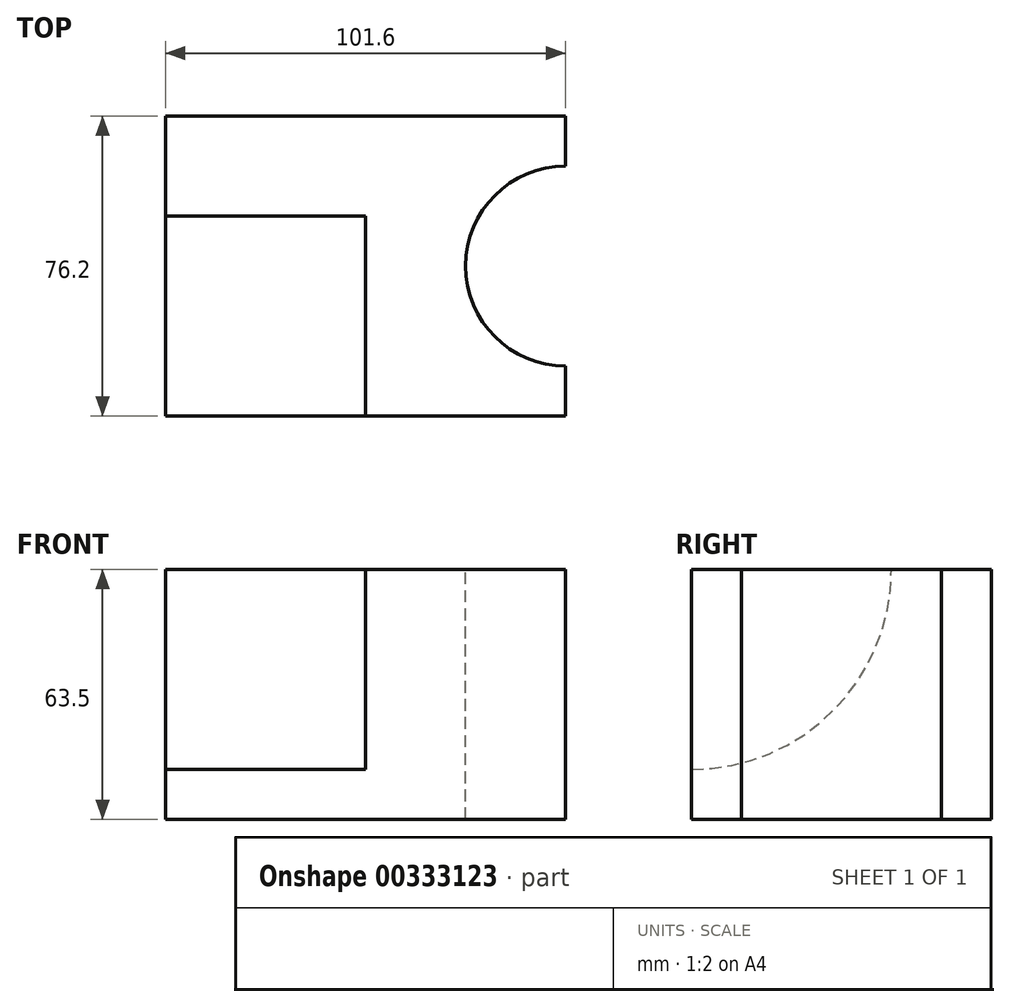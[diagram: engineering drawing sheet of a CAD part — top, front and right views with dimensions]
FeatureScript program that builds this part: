
annotation { "Feature Type Name" : "Feature", "Feature Type Description" : "" }
export const myFeature = defineFeature(function(context is Context, id is Id, definition is map)
    precondition{}
    {
        {
            var Q0;
            Q0=qCreatedBy(makeId("Front.planeOp"),FACE);
            var sketch = newSketch(context, id + "F0", { "sketchPlane" : qUnion([Q0])});
            skLineSegment(sketch, "E0", {"start": v(-68.3, 2.01) * mm, "end": v(-68.3, -61.49) * mm});
            skLineSegment(sketch, "E1", {"start": v(-68.3, -61.49) * mm, "end": v(33.3, -61.49) * mm});
            skLineSegment(sketch, "E2", {"start": v(33.3, -61.49) * mm, "end": v(33.3, 2.01) * mm});
            skLineSegment(sketch, "E3", {"start": v(33.3, 2.01) * mm, "end": v(-68.3, 2.01) * mm});
            skSolve(sketch);
        }
        {
            var Q0;
            Q0=makeQuery(id+"F0.imprint","IMPRINT",FACE,{"disambiguationData":[TD([[makeQuery(id+"F0.imprint","IMPRINT",EDGE,{"derivedFrom":sQuery(id+"F0.wireOp",EDGE,"E0")}),1.0]])]});
            extrude(context, id + "F1", {"entities" : qUnion([Q0]), "depth" : 76.2 * mm});
        }
        {
            var Q0;
            Q0=makeQuery(id+"F1.opExtrude","SWEPT_FACE",FACE,{"disambiguationData":[OSD([sQuery(id+"F0.wireOp",EDGE,"E3")])]});
            var sketch = newSketch(context, id + "F2", { "sketchPlane" : qUnion([Q0])});
            skArc(sketch, "E4", {"start": v(33.3, -12.7) * mm, "mid": v(7.9, -38.1) * mm, "end": v(33.3, -63.5) * mm});
            skSolve(sketch);
        }
        {
            var Q0;
            Q0 = qSketchRegion(id + "F2", true);
            var Q1;
            {var subQ0=sQuery(id+"F2.wireOp",EDGE,"E4");Q1=makeQuery(id+"F2.imprint","IMPRINT",FACE,{"disambiguationData":[TD([[makeQuery(id+"F2.imprint","IMPRINT",EDGE,{"derivedFrom":subQ0}),1.0]])]});}
            extrude(context, id + "F3", {"entities" : qUnion([Q0, Q1]), "operationType" : NewBodyOperationType.REMOVE, "oppositeDirection" : true, "depth" : 63.5 * mm});
        }
        {
            var Q0;
            Q0=makeQuery(id+"F1.opExtrude","SWEPT_FACE",FACE,{"disambiguationData":[OSD([sQuery(id+"F0.wireOp",EDGE,"E0")])]});
            var sketch = newSketch(context, id + "F4", { "sketchPlane" : qUnion([Q0])});
            skArc(sketch, "E5", {"start": v(25.4, 2.01) * mm, "mid": v(40.28, -33.91) * mm, "end": v(76.2, -48.79) * mm});
            skSolve(sketch);
        }
        {
            var Q0;
            Q0 = qSketchRegion(id + "F4", true);
            var Q1;
            {var subQ0=sQuery(id+"F4.wireOp",EDGE,"E5");Q1=makeQuery(id+"F4.imprint","IMPRINT",FACE,{"disambiguationData":[TD([[makeQuery(id+"F4.imprint","IMPRINT",EDGE,{"derivedFrom":subQ0}),1.0]])]});}
            extrude(context, id + "F5", {"entities" : qUnion([Q0, Q1]), "operationType" : NewBodyOperationType.REMOVE, "oppositeDirection" : true, "depth" : 50.8 * mm});
        }
    });
